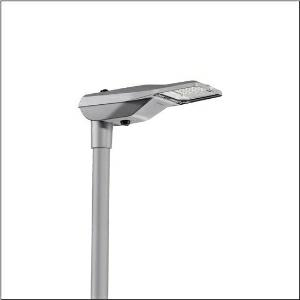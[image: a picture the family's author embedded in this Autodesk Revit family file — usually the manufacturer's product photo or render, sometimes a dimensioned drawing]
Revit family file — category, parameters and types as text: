
# Revit family: streetlight_sl_21_iq_micro___st0_8a_5xe1c31y08cb_ba99
name_source: partatom
category: Lighting Fixtures
units: mm (PartAtom-declared; Revit-internal decimal feet)

## family parameters
Cut with Voids When Loaded = No
Host = Face
Light Source = No
Part Type = Normal
Room Calculation Point = No
Round Connector Dimension = Use Diameter
Shared = No

## types (1)
- --- (1 x LED, 2880 lm, 19.1 W, 3000K)
    Apparent Load = 19 VA
    CIE Flux Codes = 38 75 97 100 100
    Color Rendering = 70
    Color Temperature = 3000K
    Default Elevation = 1800 mm
    Description = Streetlight SL 21 iQ micro, mast luminaire, primary light control with lens, of PMMA, primary optical cover: cover, of toughened safety glass, transparent, light distribution: ST0.8a, light emission: direct distribution, primary light characteristic: asymmetric, installation type: post-top, side-entry, LED, High Power LED, rated luminous flux: 2.880lm, luminous efficacy: 151lm/W, light colour: 730, colour temperature: 3000K, control gear: iQ-Street Remote, D4i with power reduction, control: pre-setting: logarithmic dimming characteristic, Street-Remote, Auto-Match, Temp-Guard, Lumen-Switch, Night-Set, Smart-Wire, Light-Fading, Desk-Remote (wireless, voltage-free reading and setting of iQ features in the workshop via application-optimized NFC function/RFID function), optimised constant luminous flux control (CLO 2.0), mains connection: 220..240V, AC, 50/60Hz, start of lifetime: 19W, end of service life: 20W, reduction: 9W, luminaire housing, of diecast aluminium, powder-coated, SITECO metallic grey (DB 702S), corrosivity category C5 high according to DIN EN ISO 12944, please order mast flange separately, inclination adjustable: 0°, 5°, 10°, 15°, sealing non-destructively replaceable, multi-level sealing system, length: 528mm, width: 235mm, height: 110mm, mast flange for spigot size: 42mm (side-entry): 5XC10008XM4, 60/48mm (side-entry/post-top): 5XC10108XM2, 76/60mm (side-entry/post-top): 5XC10108XM1, mounting height: 4..8m, Smart Interface below and above, protection rating (complete): IP66, insulation class (complete): insulation class II (safety insulation), certification: CE, ENEC, ENEC+, VDE, impact resistance: IK10, permissible operating ambient temperature for outdoor applications: -40..+50°C, standard-compliant lighting for roads and squares, packaging unit: 1 piece

Light Distribution: ST0.8a
    Height = 110 mm
    Lamp = 1 x LED
    Lamp Light Flux = 2880 lm
    Lamp Power = 19.1 W
    Lamp count = 1
    Length = 528 mm
    Luminous efficacy = 151 lm/W
    Manufacturer = Siteco
    ModVariant = No
    Model = 5XE1C31Y08CB
    Number of Poles = 1
    OnlyDefault = Yes
    Power Factor = 1
    Product Name = Streetlight SL 21 iQ micro | ST0.8a
    Product group = mast luminaire | pylon top
    ProductGroupID = 6100
    Protection Class = Protection class II
    Protection Degree = IP 66
    RLX_Detail_Level = 1
    RLX_Emergency_Light_Flux = 0 lm
    RLX_Emergency_Type = 0
    RLX_Emergency_Type_DB = No
    RlxData = <blob elided: 99361 chars, md5=3af360e3>
    Socket = socket
    Standby Power = 0 W
    System Light Flux = 2880 lm
    System Power = 19 W
    Type Comments = factory setting: luminous flux: 100 % | dim-lin: 254 | 387 mA
    Type Image = l_1007239.jpg
    URL = http://relux.com
    VarID = @adj_113547
    Voltage = 0 V
    Weight = 0.00 kg
    Width = 235 mm

## geometry (parser evidence)
native form markers: Blend x4, Sweep x9
no freeform markers — native parametric forms only
